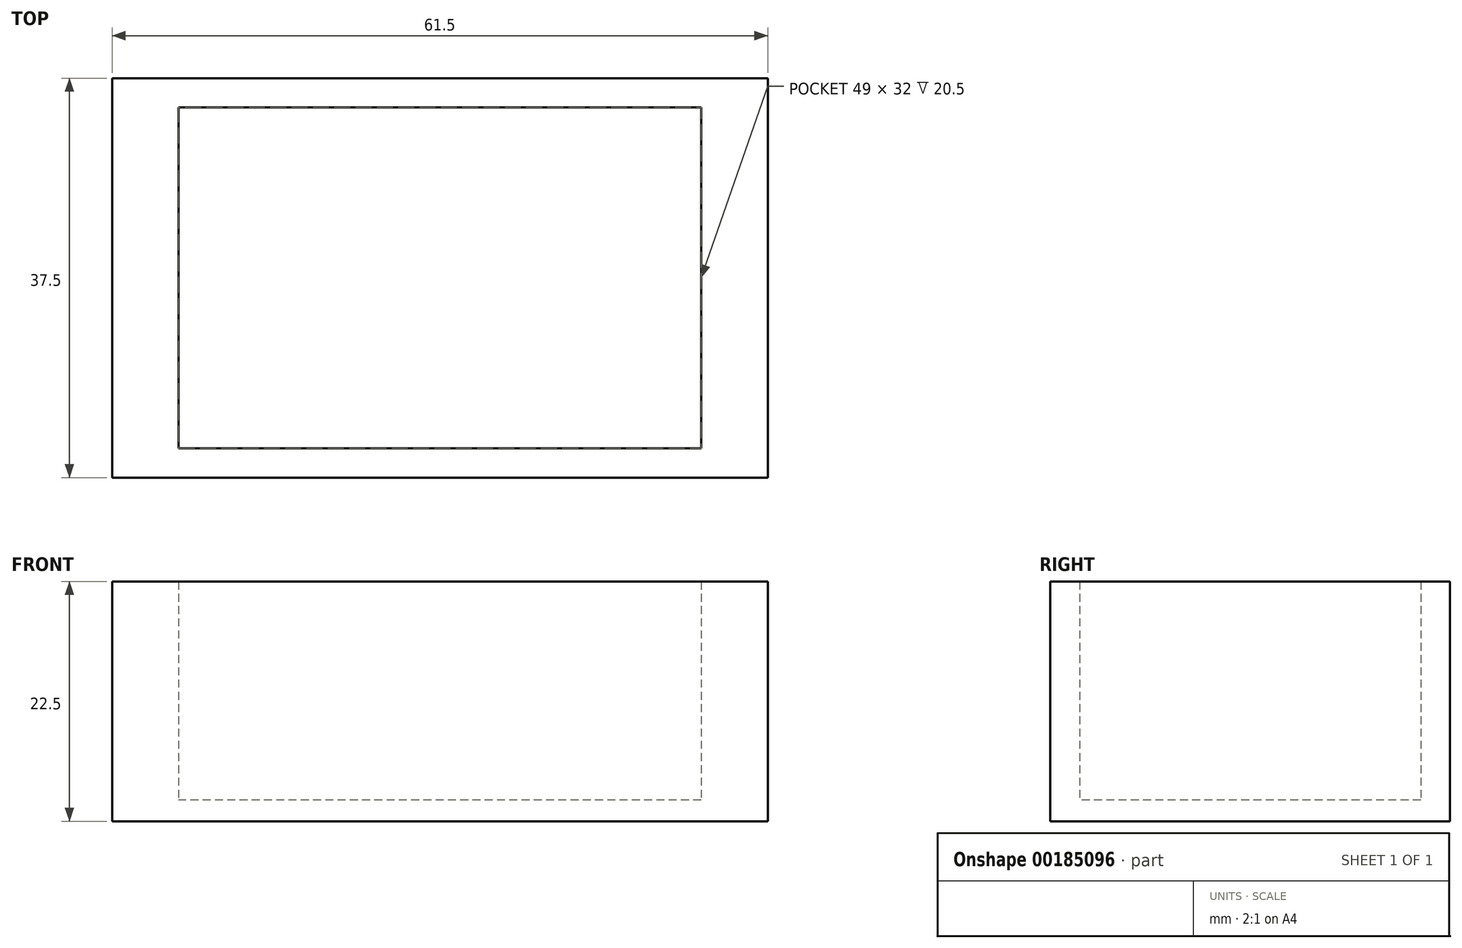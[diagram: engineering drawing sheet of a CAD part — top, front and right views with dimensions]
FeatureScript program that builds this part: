
annotation { "Feature Type Name" : "Feature", "Feature Type Description" : "" }
export const myFeature = defineFeature(function(context is Context, id is Id, definition is map)
    precondition{}
    {
        {
            var Q0;
            Q0=qCreatedBy(makeId("Top.planeOp"),FACE);
            var sketch = newSketch(context, id + "F0", { "sketchPlane" : qUnion([Q0])});
            skLineSegment(sketch, "E0.bottom", {"start": v(24.5, 16) * mm, "end": v(-24.5, 16) * mm});
            skLineSegment(sketch, "E0.top", {"start": v(24.5, -16) * mm, "end": v(-24.5, -16) * mm});
            skLineSegment(sketch, "E0.left", {"start": v(24.5, 16) * mm, "end": v(24.5, -16) * mm});
            skLineSegment(sketch, "E0.right", {"start": v(-24.5, 16) * mm, "end": v(-24.5, -16) * mm});
            skPoint(sketch, "E0.middle", {"position": v(0, 0) * mm});
            skLineSegment(sketch, "E1.bottom", {"start": v(30.75, 18.75) * mm, "end": v(-30.75, 18.75) * mm});
            skLineSegment(sketch, "E1.top", {"start": v(30.75, -18.75) * mm, "end": v(-30.75, -18.75) * mm});
            skLineSegment(sketch, "E1.left", {"start": v(30.75, 18.75) * mm, "end": v(30.75, -18.75) * mm});
            skLineSegment(sketch, "E1.right", {"start": v(-30.75, 18.75) * mm, "end": v(-30.75, -18.75) * mm});
            skSolve(sketch);
        }
        {
            var Q0;
            Q0=makeQuery(id+"F0.imprint","IMPRINT",FACE,{"disambiguationData":[TD([[makeQuery(id+"F0.imprint","IMPRINT",EDGE,{"derivedFrom":sQuery(id+"F0.wireOp",EDGE,"E0.bottom")}),-1.0]])]});
            extrude(context, id + "F1", {"entities" : qUnion([Q0]), "depth" : 20.5 * mm});
        }
        {
            var Q0;
            Q0=makeQuery(id+"F1.opExtrude","CAP_FACE",FACE,{"disambiguationData":[OSD([sQuery(id+"F0.wireOp",EDGE,"E0.bottom"),sQuery(id+"F0.wireOp",EDGE,"E0.top"),sQuery(id+"F0.wireOp",EDGE,"E0.left"),sQuery(id+"F0.wireOp",EDGE,"E0.right"),sQuery(id+"F0.wireOp",EDGE,"E1.bottom"),sQuery(id+"F0.wireOp",EDGE,"E1.top"),sQuery(id+"F0.wireOp",EDGE,"E1.left"),sQuery(id+"F0.wireOp",EDGE,"E1.right")])],"isStart":true});
            var sketch = newSketch(context, id + "F2", { "sketchPlane" : qUnion([Q0])});
            skLineSegment(sketch, "E2.bottom", {"start": v(-30.75, 18.75) * mm, "end": v(30.75, 18.75) * mm});
            skLineSegment(sketch, "E2.top", {"start": v(-30.75, -18.75) * mm, "end": v(30.75, -18.75) * mm});
            skLineSegment(sketch, "E2.left", {"start": v(-30.75, 18.75) * mm, "end": v(-30.75, -18.75) * mm});
            skLineSegment(sketch, "E2.right", {"start": v(30.75, 18.75) * mm, "end": v(30.75, -18.75) * mm});
            skSolve(sketch);
        }
        {
            var Q0;
            Q0 = qSketchRegion(id + "F2", true);
            extrude(context, id + "F3", {"entities" : qUnion([Q0]), "operationType" : NewBodyOperationType.ADD, "depth" : 2 * mm});
        }
    });
